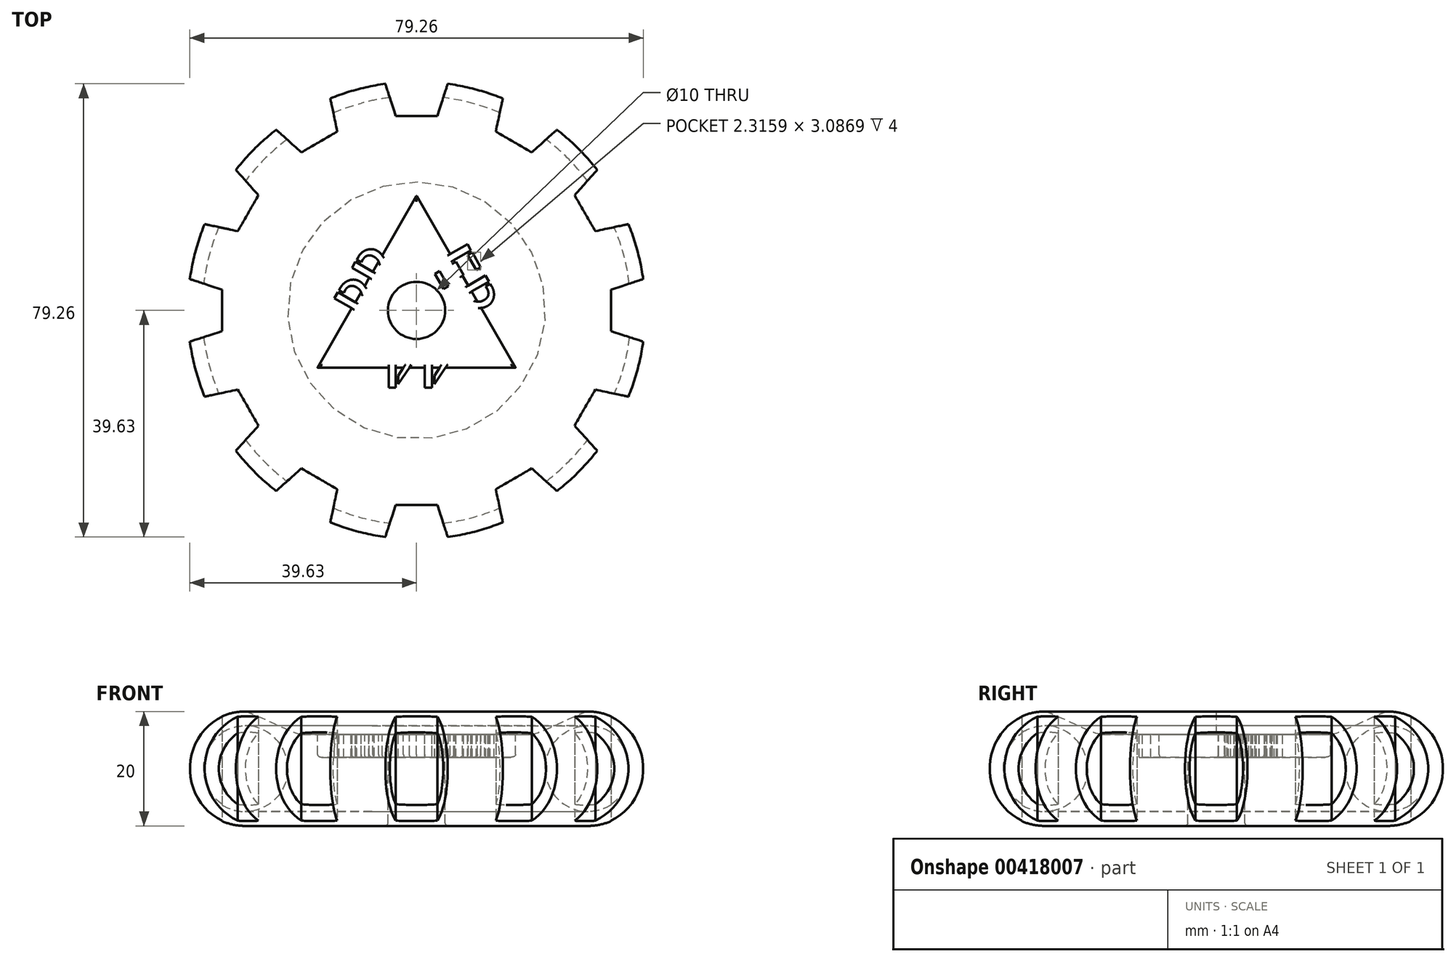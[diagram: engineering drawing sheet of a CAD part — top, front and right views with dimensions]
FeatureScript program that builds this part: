
annotation { "Feature Type Name" : "Feature", "Feature Type Description" : "" }
export const myFeature = defineFeature(function(context is Context, id is Id, definition is map)
    precondition{}
    {
        {
            assignVariable(context, id + "F0", {"name" : "diametre_jeton", "anyValue" : 80});
        }
        {
            assignVariable(context, id + "F1", {"name" : "epaisseur_jeton", "anyValue" : getVariable(context, 'diametre_jeton') * 0.2});
        }
        {
            assignVariable(context, id + "F2", {"name" : "profondeur_lettre", "anyValue" : floor(getVariable(context, 'epaisseur_jeton') / 2)});
        }
        {
            var Q0;
            Q0=qCreatedBy(makeId("Front.planeOp"),FACE);
            var sketch = newSketch(context, id + "F3", { "sketchPlane" : qUnion([Q0])});
            skLineSegment(sketch, "E0.bottom", {"start": v(0, 0) * mm, "end": v(-30, 0) * mm});
            skLineSegment(sketch, "E0.left", {"start": v(0, 0) * mm, "end": v(0, 16) * mm});
            skArc(sketch, "E1", {"start": v(-30, 20) * mm, "mid": v(-40, 10) * mm, "end": v(-30, 0) * mm});
            skPoint(sketch, "E2", {"position": v(0, 16) * mm});
            skPoint(sketch, "E3", {"position": v(-20, 16) * mm});
            skLineSegment(sketch, "E4", {"start": v(0, 16) * mm, "end": v(-20, 16) * mm});
            skFitSpline(sketch, "E5", {"points": [v(-30, 20) * mm, v(-20, 16) * mm], "startDerivative": vector(3.41, -0.02) * mm, "endDerivative": vector(4.32, 0.11) * mm});
            skSolve(sketch);
        }
        {
            var Q0;
            Q0=makeQuery(id+"F3.imprint","IMPRINT",FACE,{"disambiguationData":[TD([[makeQuery(id+"F3.imprint","IMPRINT",EDGE,{"derivedFrom":sQuery(id+"F3.wireOp",EDGE,"E0.bottom")}),-1.0]])]});
            var Q1;
            Q1=sQuery(id+"F3.wireOp",EDGE,"E0.left");
            revolve(context, id + "F4", {"entities" : qUnion([Q0]), "axis" : qUnion([Q1]), "revolveType" : RevolveType.FULL});
        }
        {
            var Q0;
            Q0=qCreatedBy(makeId("Front.planeOp"),FACE);
            var sketch = newSketch(context, id + "F5", { "sketchPlane" : qUnion([Q0])});
            skCircle(sketch, "E6", {"center": v(-30, 10) * mm, "radius": 7.5 * mm});
            skSolve(sketch);
        }
        {
            var Q0;
            Q0=qCreatedBy(makeId("Top.planeOp"),FACE);
            var Q1;
            Q1=sQuery(id+"F3.wireOp",VERTEX,"E5.start");
            cPlane(context, id + "F6", {"entities" : qUnion([Q0, Q1]), "cplaneType" : CPlaneType.PLANE_POINT, "offset" : 10.8 * mm, "width" : 150 * mm, "height" : 150 * mm});
        }
        {
            var Q0;
            Q0=qCreatedBy(id+"F6.planeOp",FACE);
            var sketch = newSketch(context, id + "F7", { "sketchPlane" : qUnion([Q0])});
            skCircle(sketch, "E7", {"center": v(0, 0) * mm, "radius": 5 * mm});
            skCircle(sketch, "E8.cCircle", {"center": v(0, 0) * mm, "radius": 10 * mm, "construction": true});
            skLineSegment(sketch, "E8.0", {"start": v(0, 20) * mm, "end": v(17.32, -10) * mm});
            skLineSegment(sketch, "E8.1", {"start": v(17.32, -10) * mm, "end": v(-17.32, -10) * mm});
            skLineSegment(sketch, "E8.2", {"start": v(-17.32, -10) * mm, "end": v(0, 20) * mm});
            skPoint(sketch, "E8.0.midPoint", {"position": v(8.66, 5) * mm});
            skText(sketch, "E9", { "text": "PP", "fontName": "AllertaStencil-Regular.ttf"});
            skLineSegment(sketch, "E10", {"start": v(0, 0) * mm, "end": v(-14.99, 8.65) * mm, "construction": true});
            skLineSegment(sketch, "E11", {"start": v(0, 0) * mm, "end": v(15.87, 9.16) * mm, "construction": true});
            skLineSegment(sketch, "E12", {"start": v(0, 0) * mm, "end": v(0, -15.53) * mm, "construction": true});
            skText(sketch, "E13", { "text": "ER", "fontName": "AllertaStencil-Regular.ttf"});
            skText(sketch, "E14", { "text": "44", "fontName": "AllertaStencil-Regular.ttf"});
            const initialGuessF7  = {"E9": [-0.00833, -0.00243, 0.5, 0.86603, 0.0075], "E13": [0.00192, 0.00867, 0.5, -0.86603, 0.0075], "E14": [0.00633, -0.006, -1, 0, 0.0075]};
            skSetInitialGuess(sketch, initialGuessF7);
            skSolve(sketch);
        }
        {
            var Q0;
            Q0 = qSketchRegion(id + "F7", true);
            extrude(context, id + "F8", {"entities" : qUnion([Q0]), "operationType" : NewBodyOperationType.REMOVE, "oppositeDirection" : true, "depth" : (getVariable(context, 'profondeur_lettre')) * mm});
        }
        {
            var Q0;
            Q0=makeQuery(id+"F7.imprint","IMPRINT",FACE,{"disambiguationData":[TD([[makeQuery(id+"F7.imprint","IMPRINT",EDGE,{"derivedFrom":sQuery(id+"F7.wireOp",EDGE,"E7")}),1.0]])]});
            var Q1;
            Q1=makeQuery(id+"F4.opRevolve","SWEPT_FACE",FACE,{"disambiguationData":[OSD([sQuery(id+"F3.wireOp",EDGE,"E0.bottom")])]});
            var Q2;
            Q2=makeQuery(id+"F4.opRevolve","SWEPT_FACE",FACE,{"disambiguationData":[OSD([sQuery(id+"F3.wireOp",EDGE,"E0.bottom")])]});
            extrude(context, id + "F9", {"entities" : qUnion([Q0, Q1]), "operationType" : NewBodyOperationType.REMOVE, "oppositeDirection" : true, "endBoundEntityFace" : qUnion([Q2]), "depth" : 100 * mm});
        }
        {
            var Q0;
            Q0=makeQuery(id+"F4.opRevolve","SWEPT_EDGE",EDGE,{"disambiguationData":[OSD([sQuery(id+"F3.wireOp",EDGE,"E4"),sQuery(id+"F3.wireOp",EDGE,"suWCrNEA-gwf6-b7T6-fGyV-5P04xxjI4HWT")])]});
            var Q1;
            Q1=makeQuery(id+"F8.boolean.opBoolean","INTERSECT",EDGE,{"derivedFrom":[makeQuery(id+"F4.opRevolve","SWEPT_FACE",FACE,{"disambiguationData":[OSD([sQuery(id+"F3.wireOp",EDGE,"E4")])]}),makeQuery(id+"F8.opExtrude","SWEPT_FACE",FACE,{"disambiguationData":[OSD([sQuery(id+"F7.wireOp",EDGE,"E7")])]})]});
            var Q2;
            Q2=makeQuery(id+"F8.boolean.opBoolean","COPY",EDGE,{"derivedFrom":makeQuery(id+"F8.opExtrude","CAP_EDGE",EDGE,{"disambiguationData":[OSD([sQuery(id+"F7.wireOp",EDGE,"E7")])],"isStart":false})});
            var Q3;
            Q3=makeQuery(id+"F8.boolean.opBoolean","COPY",EDGE,{"derivedFrom":makeQuery(id+"F8.opExtrude","CAP_EDGE",EDGE,{"disambiguationData":[OSD([sQuery(id+"F7.wireOp",EDGE,"E8.0")])],"isStart":false})});
            var Q4;
            Q4=makeQuery(id+"F8.boolean.opBoolean","COPY",EDGE,{"derivedFrom":makeQuery(id+"F8.opExtrude","CAP_EDGE",EDGE,{"disambiguationData":[OSD([sQuery(id+"F7.wireOp",EDGE,"E8.2")])],"isStart":false})});
            var Q5;
            Q5=makeQuery(id+"F8.boolean.opBoolean","COPY",EDGE,{"derivedFrom":makeQuery(id+"F8.opExtrude","CAP_EDGE",EDGE,{"disambiguationData":[OSD([sQuery(id+"F7.wireOp",EDGE,"E8.1")])],"isStart":false})});
            var Q6;
            {var subQ0=sQuery(id+"F3.wireOp",EDGE,"E0.bottom");Q6=makeQuery(id+"F9.boolean.opBoolean","INTERSECT",EDGE,{"derivedFrom":[makeQuery(id+"F4.opRevolve","SWEPT_FACE",FACE,{"disambiguationData":[OSD([subQ0])]}),makeQuery(id+"F9.opExtrude","CAP_FACE",FACE,{"disambiguationData":[OSD([subQ0])],"isStart":true}),makeQuery(id+"F9.opExtrude","SWEPT_FACE",FACE,{"disambiguationData":[OSD([sQuery(id+"F7.wireOp",EDGE,"E7")])]})]});}
            fillet(context, id + "F10", {"entities" : qUnion([Q0, Q1, Q2, Q3, Q4, Q5, Q6]), "radius" : 0.5 * mm, "tangentPropagation" : true, "allowEdgeOverflow" : false});
        }
        {
            var Q0;
            Q0 = qSketchRegion(id + "F5", true);
            var Q1;
            Q1=sQuery(id+"F3.wireOp",EDGE,"E0.left");
            revolve(context, id + "F11", {"entities" : qUnion([Q0]), "axis" : qUnion([Q1]), "revolveType" : RevolveType.FULL});
        }
        {
            var Q0;
            Q0=qCreatedBy(makeId("Top.planeOp"),FACE);
            var sketch = newSketch(context, id + "F12", { "sketchPlane" : qUnion([Q0])});
            skCircle(sketch, "E15.cCircle", {"center": v(0, 39) * mm, "radius": 5 * mm, "construction": true});
            skLineSegment(sketch, "E15.0", {"start": v(3.63, 34) * mm, "end": v(-3.63, 34) * mm});
            skLineSegment(sketch, "E15.1", {"start": v(-3.63, 34) * mm, "end": v(-5.88, 40.9) * mm});
            skLineSegment(sketch, "E15.2", {"start": v(-5.88, 40.9) * mm, "end": v(0, 45.18) * mm});
            skLineSegment(sketch, "E15.3", {"start": v(0, 45.18) * mm, "end": v(5.88, 40.9) * mm});
            skLineSegment(sketch, "E15.4", {"start": v(5.88, 40.9) * mm, "end": v(3.63, 34) * mm});
            skPoint(sketch, "E15.0.midPoint", {"position": v(0, 34) * mm});
            skSolve(sketch);
        }
        {
            var Q0;
            Q0=makeQuery(id+"F12.imprint","IMPRINT",FACE,{"disambiguationData":[TD([[makeQuery(id+"F12.imprint","IMPRINT",EDGE,{"derivedFrom":sQuery(id+"F12.wireOp",EDGE,"E15.0")}),-1.0]])]});
            extrude(context, id + "F13", {"entities" : qUnion([Q0]), "endBound" : BoundingType.SYMMETRIC, "depth" : 100 * mm});
        }
        {
            var Q0;
            Q0=makeQuery(id+"F13.opExtrude","SWEPT_BODY",BODY,{"disambiguationData":[OSD([sQuery(id+"F12.wireOp",EDGE,"E15.0"),sQuery(id+"F12.wireOp",EDGE,"E15.1"),sQuery(id+"F12.wireOp",EDGE,"E15.2"),sQuery(id+"F12.wireOp",EDGE,"E15.3"),sQuery(id+"F12.wireOp",EDGE,"E15.4")])]});
            var Q1;
            Q1=sQuery(id+"F3.wireOp",EDGE,"E0.left");
            circularPattern(context, id + "F14", {"operationType" : NewBodyOperationType.REMOVE, "entities" : qUnion([Q0]), "axis" : qUnion([Q1]), "angle" : 360 * degree, "instanceCount" : 12, "equalSpace" : true, "isCentered" : true});
        }
    });
